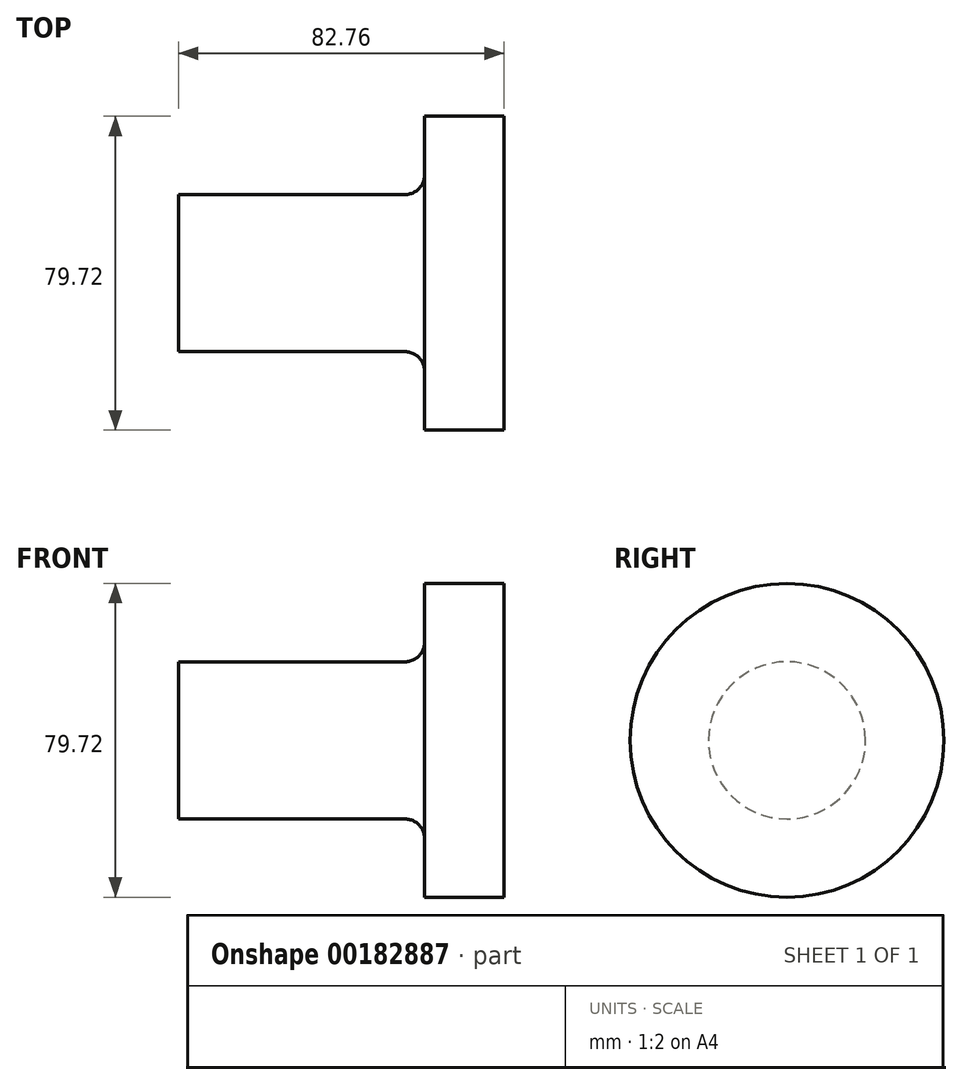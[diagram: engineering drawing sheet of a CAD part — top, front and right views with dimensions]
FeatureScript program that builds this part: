
annotation { "Feature Type Name" : "Feature", "Feature Type Description" : "" }
export const myFeature = defineFeature(function(context is Context, id is Id, definition is map)
    precondition{}
    {
        {
            var Q0;
            Q0=qCreatedBy(makeId("Front.planeOp"),FACE);
            var sketch = newSketch(context, id + "F0", { "sketchPlane" : qUnion([Q0])});
            skLineSegment(sketch, "E0.bottom", {"start": v(0, 0) * mm, "end": v(82.76, 0) * mm});
            skLineSegment(sketch, "E0.top", {"start": v(0, 19.97) * mm, "end": v(57.57, 19.97) * mm});
            skLineSegment(sketch, "E0.left", {"start": v(0, 0) * mm, "end": v(0, 19.97) * mm});
            skLineSegment(sketch, "E0.right", {"start": v(82.76, 0) * mm, "end": v(82.76, 19.97) * mm});
            skLineSegment(sketch, "E1", {"start": v(0, 0) * mm, "end": v(-27.59, 0) * mm, "construction": true});
            skLineSegment(sketch, "E2", {"start": v(82.76, 19.97) * mm, "end": v(82.76, 39.86) * mm});
            skLineSegment(sketch, "E3", {"start": v(82.76, 39.86) * mm, "end": v(62.57, 39.86) * mm});
            skLineSegment(sketch, "E4", {"start": v(62.57, 39.86) * mm, "end": v(62.57, 24.97) * mm});
            skPoint(sketch, "E5.visualSharp", {"position": v(62.57, 19.97) * mm});
            skArc(sketch, "E5.filletArc", {"start": v(57.57, 19.97) * mm, "mid": v(61.1, 21.44) * mm, "end": v(62.57, 24.97) * mm});
            skSolve(sketch);
        }
        {
            var Q0;
            Q0=makeQuery(id+"F0.imprint","IMPRINT",FACE,{"disambiguationData":[TD([[makeQuery(id+"F0.imprint","IMPRINT",EDGE,{"derivedFrom":sQuery(id+"F0.wireOp",EDGE,"E0.bottom")}),1.0]])]});
            var Q1;
            Q1=sQuery(id+"F0.wireOp",EDGE,"E1");
            revolve(context, id + "F1", {"entities" : qUnion([Q0]), "axis" : qUnion([Q1]), "revolveType" : RevolveType.FULL});
        }
    });
